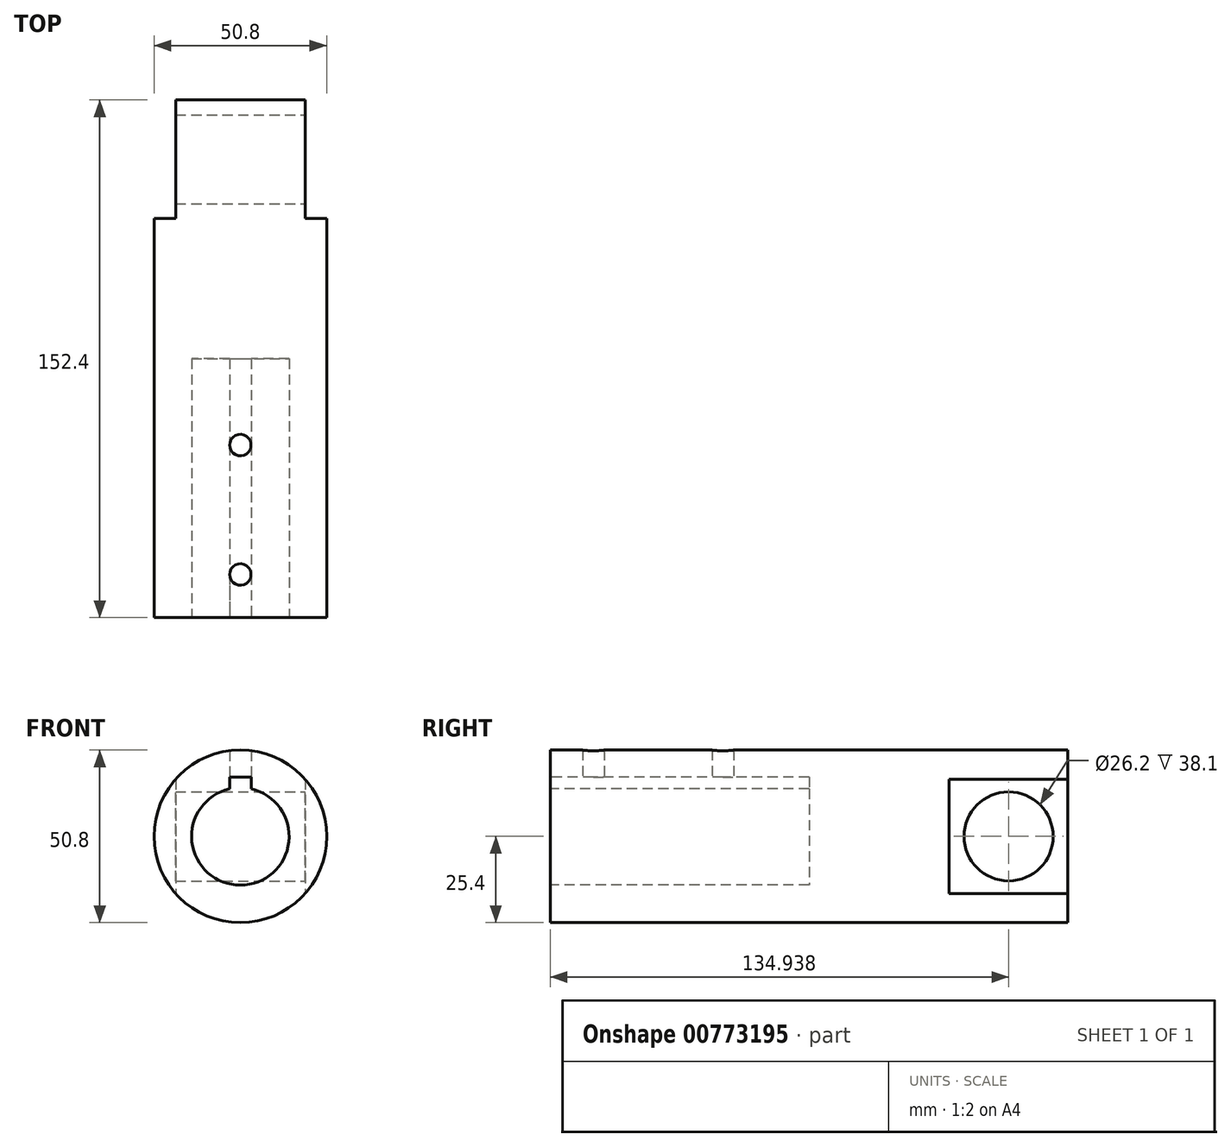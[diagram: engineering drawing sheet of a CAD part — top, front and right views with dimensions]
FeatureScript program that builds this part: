
annotation { "Feature Type Name" : "Feature", "Feature Type Description" : "" }
export const myFeature = defineFeature(function(context is Context, id is Id, definition is map)
    precondition{}
    {
        {
            var Q0;
            Q0=qCreatedBy(makeId("Front.planeOp"),FACE);
            var sketch = newSketch(context, id + "F0", { "sketchPlane" : qUnion([Q0])});
            skCircle(sketch, "E0", {"center": v(0, 0) * mm, "radius": 25.4 * mm});
            skSolve(sketch);
        }
        {
            var Q0;
            Q0=makeQuery(id+"F0.imprint","IMPRINT",FACE,{"disambiguationData":[TD([[makeQuery(id+"F0.imprint","IMPRINT",EDGE,{"derivedFrom":sQuery(id+"F0.wireOp",EDGE,"E0")}),1.0]])]});
            extrude(context, id + "F1", {"entities" : qUnion([Q0]), "oppositeDirection" : true, "depth" : 152.4 * mm, "offsetDistance" : 25.4 * mm});
        }
        {
            var Q0;
            Q0=makeQuery(id+"F1.opExtrude","CAP_FACE",FACE,{"disambiguationData":[OSD([sQuery(id+"F0.wireOp",EDGE,"E0")])],"isStart":true});
            var sketch = newSketch(context, id + "F2", { "sketchPlane" : qUnion([Q0])});
            skCircle(sketch, "E1", {"center": v(0, 0) * mm, "radius": 14.35 * mm});
            skLineSegment(sketch, "E2.bottom", {"start": v(-3.18, 17.46) * mm, "end": v(3.17, 17.46) * mm});
            skLineSegment(sketch, "E2.top", {"start": v(-3.18, 11.11) * mm, "end": v(3.17, 11.11) * mm});
            skLineSegment(sketch, "E2.left", {"start": v(-3.18, 17.46) * mm, "end": v(-3.18, 11.11) * mm});
            skLineSegment(sketch, "E2.right", {"start": v(3.17, 17.46) * mm, "end": v(3.17, 11.11) * mm});
            skSolve(sketch);
        }
        {
            var Q0;
            {var subQ5=sQuery(id+"F2.wireOp",EDGE,"E2.top");Q0=makeQuery(id+"F2.imprint","IMPRINT",FACE,{"disambiguationData":[TD([[makeQuery(id+"F2.imprint","IMPRINT",EDGE,{"derivedFrom":subQ5}),-1.0]])]});}
            var Q1;
            {var subQ5=sQuery(id+"F2.wireOp",EDGE,"E2.top");Q1=makeQuery(id+"F2.imprint","IMPRINT",FACE,{"disambiguationData":[TD([[makeQuery(id+"F2.imprint","IMPRINT",EDGE,{"derivedFrom":subQ5}),1.0]])]});}
            var Q2;
            {var subQ5=sQuery(id+"F2.wireOp",EDGE,"E2.bottom");Q2=makeQuery(id+"F2.imprint","IMPRINT",FACE,{"disambiguationData":[TD([[makeQuery(id+"F2.imprint","IMPRINT",EDGE,{"derivedFrom":subQ5}),-1.0]])]});}
            extrude(context, id + "F3", {"entities" : qUnion([Q0, Q1, Q2]), "operationType" : NewBodyOperationType.REMOVE, "oppositeDirection" : true, "depth" : 76.2 * mm, "offsetDistance" : 25.4 * mm});
        }
        {
            var Q0;
            Q0=makeQuery(id+"F3.boolean.opBoolean","COPY",FACE,{"derivedFrom":makeQuery(id+"F3.opExtrude","SWEPT_FACE",FACE,{"disambiguationData":[OSD([sQuery(id+"F2.wireOp",EDGE,"E2.bottom")])]})});
            var sketch = newSketch(context, id + "F4", { "sketchPlane" : qUnion([Q0])});
            skCircle(sketch, "E3", {"center": v(0, -50.8) * mm, "radius": 3.18 * mm});
            skCircle(sketch, "E4", {"center": v(0, -12.7) * mm, "radius": 3.18 * mm});
            skSolve(sketch);
        }
        {
            var Q0;
            {var subQ0=sQuery(id+"F4.wireOp",EDGE,"E4");var subQ1=sQuery(id+"F2.wireOp",EDGE,"E2.bottom");var subQ2=makeQuery(id+"F4.imprint","INTERSECT",VERTEX,{"derivedFrom":[makeQuery(id+"F3.boolean.opBoolean","COPY",EDGE,{"derivedFrom":makeQuery(id+"F3.opExtrude","SWEPT_EDGE",EDGE,{"disambiguationData":[OSD([subQ1,sQuery(id+"F2.wireOp",EDGE,"E2.left")])]})}),subQ0]});Q0=makeQuery(id+"F4.imprint","IMPRINT",FACE,{"disambiguationData":[TD([[makeQuery(id+"F4.imprint","IMPRINT",EDGE,{"disambiguationData":[TD([[subQ2,1.0]])],"derivedFrom":subQ0}),1.0]])]});}
            var Q1;
            {var subQ0=sQuery(id+"F4.wireOp",EDGE,"E3");var subQ1=sQuery(id+"F2.wireOp",EDGE,"E2.bottom");var subQ2=makeQuery(id+"F4.imprint","INTERSECT",VERTEX,{"derivedFrom":[makeQuery(id+"F3.boolean.opBoolean","COPY",EDGE,{"derivedFrom":makeQuery(id+"F3.opExtrude","SWEPT_EDGE",EDGE,{"disambiguationData":[OSD([subQ1,sQuery(id+"F2.wireOp",EDGE,"E2.left")])]})}),subQ0]});Q1=makeQuery(id+"F4.imprint","IMPRINT",FACE,{"disambiguationData":[TD([[makeQuery(id+"F4.imprint","IMPRINT",EDGE,{"disambiguationData":[TD([[subQ2,1.0]])],"derivedFrom":subQ0}),1.0]])]});}
            extrude(context, id + "F5", {"entities" : qUnion([Q0, Q1]), "operationType" : NewBodyOperationType.REMOVE, "endBound" : BoundingType.UP_TO_NEXT, "oppositeDirection" : true, "depth" : 25.4 * mm, "offsetDistance" : 25.4 * mm});
        }
        {
            var Q0;
            Q0=makeQuery(id+"F1.opExtrude","CAP_FACE",FACE,{"disambiguationData":[OSD([sQuery(id+"F0.wireOp",EDGE,"E0")])],"isStart":false});
            var sketch = newSketch(context, id + "F6", { "sketchPlane" : qUnion([Q0])});
            skCircle(sketch, "E5", {"center": v(0, 0) * mm, "radius": 25.4 * mm});
            skLineSegment(sketch, "E6", {"start": v(-19.05, 16.8) * mm, "end": v(-19.05, -16.8) * mm});
            skLineSegment(sketch, "E7", {"start": v(19.05, 16.8) * mm, "end": v(19.05, -16.8) * mm});
            skSolve(sketch);
        }
        {
            var Q0;
            {var subQ0=sQuery(id+"F6.wireOp",EDGE,"E6");Q0=makeQuery(id+"F6.imprint","IMPRINT",FACE,{"disambiguationData":[TD([[makeQuery(id+"F6.imprint","IMPRINT",EDGE,{"derivedFrom":subQ0}),-1.0]])]});}
            var Q1;
            {var subQ0=sQuery(id+"F6.wireOp",EDGE,"E7");Q1=makeQuery(id+"F6.imprint","IMPRINT",FACE,{"disambiguationData":[TD([[makeQuery(id+"F6.imprint","IMPRINT",EDGE,{"derivedFrom":subQ0}),1.0]])]});}
            extrude(context, id + "F7", {"entities" : qUnion([Q0, Q1]), "operationType" : NewBodyOperationType.REMOVE, "oppositeDirection" : true, "depth" : 34.92 * mm, "offsetDistance" : 25.4 * mm});
        }
        {
            var Q0;
            Q0=makeQuery(id+"F7.boolean.opBoolean","COPY",FACE,{"derivedFrom":makeQuery(id+"F7.opExtrude","SWEPT_FACE",FACE,{"disambiguationData":[OSD([sQuery(id+"F6.wireOp",EDGE,"E6")])]})});
            var sketch = newSketch(context, id + "F8", { "sketchPlane" : qUnion([Q0])});
            skLineSegment(sketch, "E8", {"start": v(152.4, 0) * mm, "end": v(134.94, 0) * mm, "construction": true});
            skSolve(sketch);
        }
        {
            var Q0;
            Q0=sQuery(id+"F8.wireOp",VERTEX,"E8.end");
            var Q1;
            Q1=makeQuery(id+"F1.opExtrude","SWEPT_BODY",BODY,{"disambiguationData":[OSD([sQuery(id+"F0.wireOp",EDGE,"E0")])]});
            hole(context, id + "F9", {"style" : HoleStyle.SIMPLE, "endStyle" : HoleEndStyle.THROUGH, "standardTappedOrClearance" : lookupTablePath({ "standard" : "ANSI", "fit" : "Normal (ASME)", "size" : "1", "type" : "Clearance" }), "standardBlindInLast" : lookupTablePath({ "fit" : "Free", "standard" : "ANSI", "size" : "1", "type" : "Clearance" }), "holeDiameter" : 26.2 * mm, "majorDiameter" : 25.4 * mm, "isTappedThrough" : true, "tappedDepth" : 12.7 * mm, "tapClearance" : 3, "locations" : qUnion([Q0]), "scope" : qUnion([Q1])});
        }
    });
